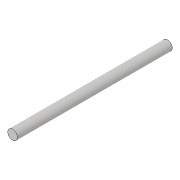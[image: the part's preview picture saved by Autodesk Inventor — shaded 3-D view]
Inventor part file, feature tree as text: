
AUTODESK INVENTOR PART (.ipt)
format: ipt  version: 2018.3 (Build 223284000, 284)  size: 70,656 bytes
history: native  units: in
note: dims shown in document units (in); Inventor stores cm internally (conversion verified against a paired STEP export)
features: extrude x1, sketch x1
ambient origin geometry x8: Origin, YZ Plane, XZ Plane, XY Plane, X Axis, Y Axis, Z Axis, Center Point
bodies: Solid1 (feature_tree)
feature tree (2):
  extrude  "Extrusion1"  Depth=8.0in TaperAngle=0.0deg
  sketch  "Sketch1"  dims[d0=0.5in d1=8.0in d2=0.0in]
